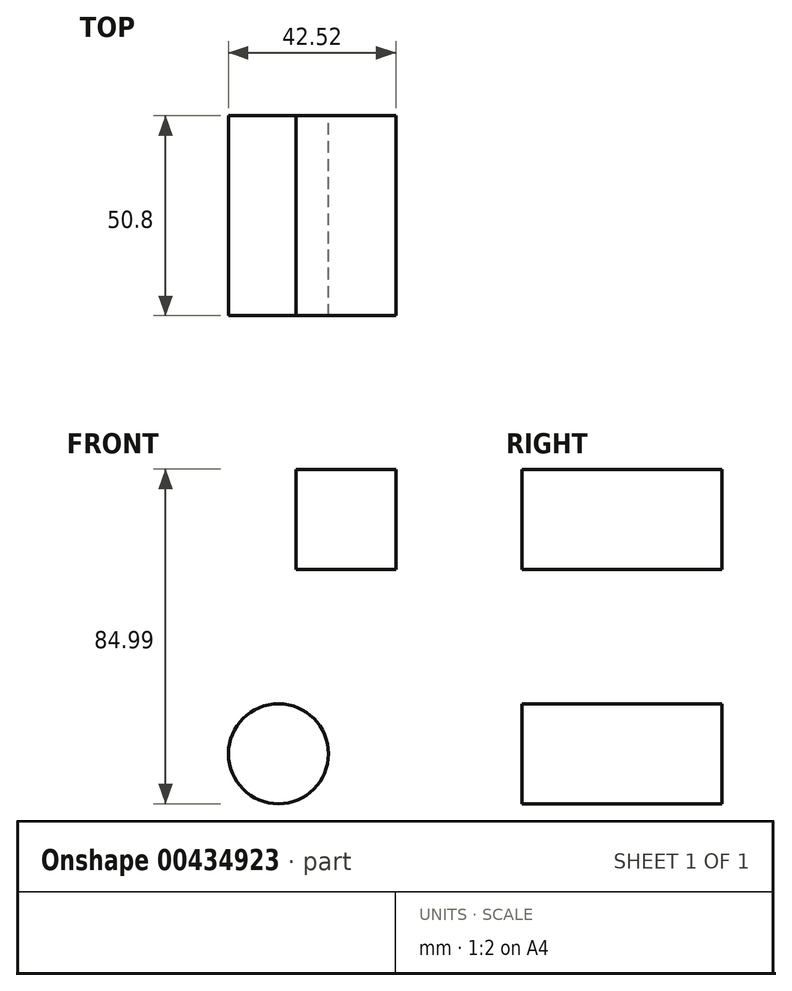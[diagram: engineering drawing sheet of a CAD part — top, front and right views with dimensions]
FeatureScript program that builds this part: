
annotation { "Feature Type Name" : "Feature", "Feature Type Description" : "" }
export const myFeature = defineFeature(function(context is Context, id is Id, definition is map)
    precondition{}
    {
        {
            var Q0;
            Q0=qCreatedBy(makeId("Front.planeOp"),FACE);
            var sketch = newSketch(context, id + "F0", { "sketchPlane" : qUnion([Q0])});
            skLineSegment(sketch, "E0", {"start": v(-6.1, 44.88) * mm, "end": v(-31.5, 44.88) * mm});
            skLineSegment(sketch, "E1", {"start": v(-31.5, 44.88) * mm, "end": v(-31.5, 19.48) * mm});
            skLineSegment(sketch, "E2", {"start": v(-31.5, 19.48) * mm, "end": v(-6.11, 19.48) * mm});
            skLineSegment(sketch, "E3", {"start": v(-6.11, 19.48) * mm, "end": v(-6.1, 44.88) * mm});
            skSolve(sketch);
        }
        {
            var Q0;
            Q0=makeQuery(id+"F0.imprint","IMPRINT",FACE,{"disambiguationData":[TD([[makeQuery(id+"F0.imprint","IMPRINT",EDGE,{"derivedFrom":sQuery(id+"F0.wireOp",EDGE,"E0")}),1.0]])]});
            extrude(context, id + "F1", {"entities" : qUnion([Q0]), "depth" : 50.8 * mm});
        }
        {
            var Q0;
            Q0=qCreatedBy(makeId("Front.planeOp"),FACE);
            var sketch = newSketch(context, id + "F2", { "sketchPlane" : qUnion([Q0])});
            skCircle(sketch, "E4", {"center": v(-35.93, -27.41) * mm, "radius": 12.7 * mm});
            skSolve(sketch);
        }
        {
            var Q0;
            Q0 = qSketchRegion(id + "F2", true);
            extrude(context, id + "F3", {"entities" : qUnion([Q0]), "depth" : 50.8 * mm});
        }
    });
